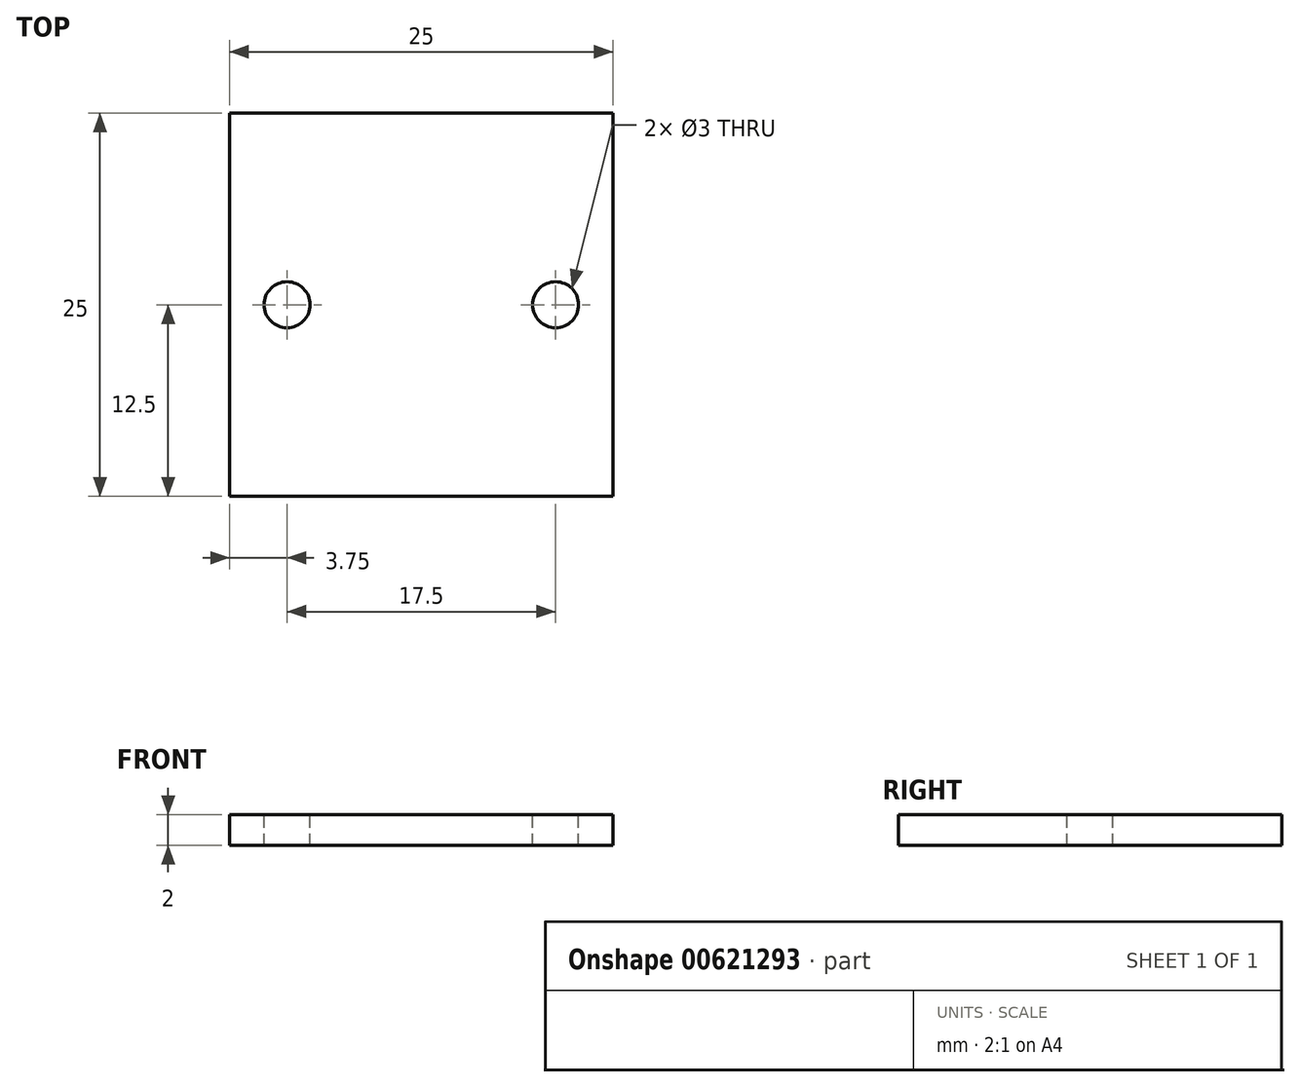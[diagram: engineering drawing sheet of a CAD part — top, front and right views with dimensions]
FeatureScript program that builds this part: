
annotation { "Feature Type Name" : "Feature", "Feature Type Description" : "" }
export const myFeature = defineFeature(function(context is Context, id is Id, definition is map)
    precondition{}
    {
        {
            var Q0;
            Q0=qCreatedBy(makeId("Top.planeOp"),FACE);
            var sketch = newSketch(context, id + "F0", { "sketchPlane" : qUnion([Q0])});
            skLineSegment(sketch, "E0.bottom", {"start": v(12.5, 12.5) * mm, "end": v(-12.5, 12.5) * mm});
            skLineSegment(sketch, "E0.top", {"start": v(12.5, -12.5) * mm, "end": v(-12.5, -12.5) * mm});
            skLineSegment(sketch, "E0.left", {"start": v(12.5, 12.5) * mm, "end": v(12.5, -12.5) * mm});
            skLineSegment(sketch, "E0.right", {"start": v(-12.5, 12.5) * mm, "end": v(-12.5, -12.5) * mm});
            skPoint(sketch, "E0.middle", {"position": v(0, 0) * mm});
            skLineSegment(sketch, "E1", {"start": v(0, 0) * mm, "end": v(-8.75, 0) * mm, "construction": true});
            skLineSegment(sketch, "E2.MirrorCS", {"start": v(0, 0) * mm, "end": v(8.75, 0) * mm, "construction": true});
            skSolve(sketch);
        }
        {
            var Q0;
            Q0 = qSketchRegion(id + "F0", true);
            extrude(context, id + "F1", {"entities" : qUnion([Q0]), "oppositeDirection" : true, "depth" : 2 * mm, "offsetDistance" : 25 * mm});
        }
        {
            var Q0;
            Q0=sQuery(id+"F0.wireOp",VERTEX,"E1.end");
            var Q1;
            Q1=sQuery(id+"F0.wireOp",VERTEX,"E2.MirrorCS.end");
            var Q2;
            Q2=makeQuery(id+"F1.opExtrude","SWEPT_BODY",BODY,{"disambiguationData":[OSD([sQuery(id+"F0.wireOp",EDGE,"E0.bottom"),sQuery(id+"F0.wireOp",EDGE,"E0.top"),sQuery(id+"F0.wireOp",EDGE,"E0.left"),sQuery(id+"F0.wireOp",EDGE,"E0.right")])]});
            hole(context, id + "F2", {"style" : HoleStyle.SIMPLE, "endStyle" : HoleEndStyle.THROUGH, "standardTappedOrClearance" : lookupTablePath({ "standard" : "ISO", "size" : "3", "type" : "Drilled" }), "standardBlindInLast" : lookupTablePath({ "standard" : "ISO", "size" : "3", "type" : "Drilled" }), "holeDiameter" : 3 * mm, "majorDiameter" : 5 * mm, "isTappedThrough" : true, "tappedDepth" : 12 * mm, "tapClearance" : 3, "locations" : qUnion([Q0, Q1]), "scope" : qUnion([Q2])});
        }
    });
